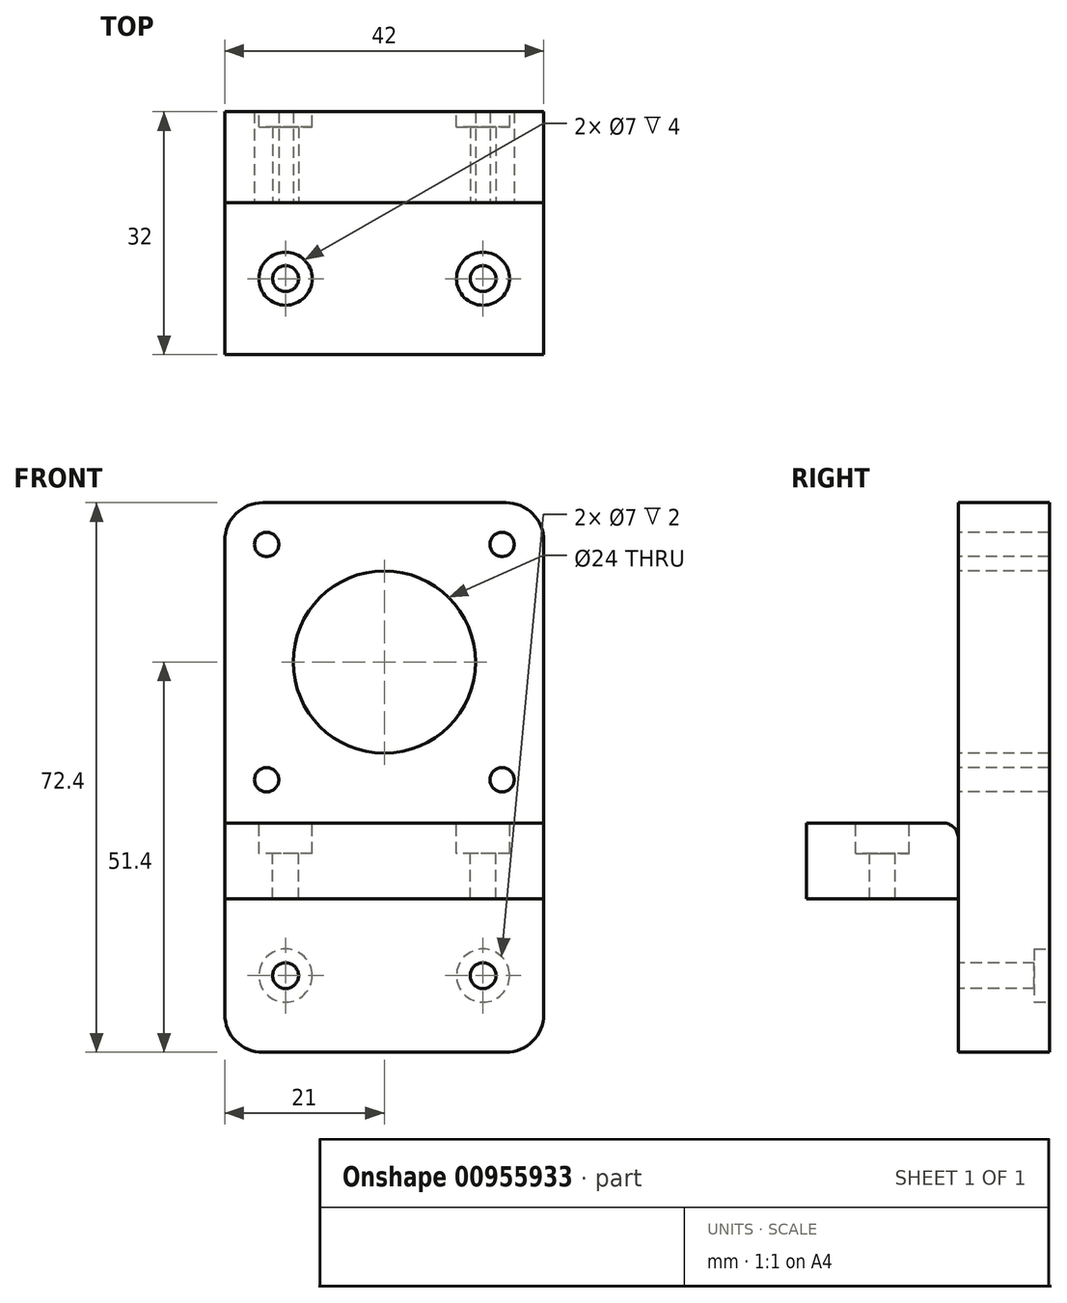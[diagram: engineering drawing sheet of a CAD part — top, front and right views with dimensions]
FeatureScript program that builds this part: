
annotation { "Feature Type Name" : "Feature", "Feature Type Description" : "" }
export const myFeature = defineFeature(function(context is Context, id is Id, definition is map)
    precondition{}
    {
        {
            var Q0;
            Q0=qCreatedBy(makeId("Front.planeOp"),FACE);
            var sketch = newSketch(context, id + "F0", { "sketchPlane" : qUnion([Q0])});
            skLineSegment(sketch, "E0.bottom", {"start": v(-21, 21) * mm, "end": v(21, 21) * mm});
            skLineSegment(sketch, "E0.left", {"start": v(-21, 21) * mm, "end": v(-21, -21) * mm});
            skLineSegment(sketch, "E0.right", {"start": v(21, 21) * mm, "end": v(21, -21) * mm});
            skPoint(sketch, "E0.middle", {"position": v(0, 0) * mm});
            skLineSegment(sketch, "E1", {"start": v(0, 0) * mm, "end": v(15.5, 0) * mm, "construction": true});
            skLineSegment(sketch, "E2", {"start": v(0, 0) * mm, "end": v(0, 15.5) * mm, "construction": true});
            skLineSegment(sketch, "E3", {"start": v(15.5, -21) * mm, "end": v(15.5, 21) * mm, "construction": true});
            skLineSegment(sketch, "E4", {"start": v(21, 15.5) * mm, "end": v(-21, 15.5) * mm, "construction": true});
            skLineSegment(sketch, "E5", {"start": v(0, 0) * mm, "end": v(-15.5, 0) * mm, "construction": true});
            skLineSegment(sketch, "E6", {"start": v(0, 0) * mm, "end": v(0, -15.5) * mm, "construction": true});
            skLineSegment(sketch, "E7", {"start": v(-15.5, 21) * mm, "end": v(-15.5, -21) * mm, "construction": true});
            skLineSegment(sketch, "E8", {"start": v(21, -15.5) * mm, "end": v(-21, -15.5) * mm, "construction": true});
            skCircle(sketch, "E9", {"center": v(-15.5, 15.5) * mm, "radius": 1.6 * mm});
            skCircle(sketch, "E10", {"center": v(15.5, 15.5) * mm, "radius": 1.6 * mm});
            skCircle(sketch, "E11", {"center": v(15.5, -15.5) * mm, "radius": 1.6 * mm});
            skCircle(sketch, "E12", {"center": v(-15.5, -15.5) * mm, "radius": 1.6 * mm});
            skLineSegment(sketch, "E13", {"start": v(-21, -21) * mm, "end": v(21, -21) * mm});
            skLineSegment(sketch, "E14.0", {"start": v(-21, -21.2) * mm, "end": v(21, -21.2) * mm});
            skLineSegment(sketch, "E15", {"start": v(21, -21.2) * mm, "end": v(21, -31.2) * mm});
            skLineSegment(sketch, "E16", {"start": v(-21, -31.2) * mm, "end": v(21, -31.2) * mm});
            skLineSegment(sketch, "E17.bottom", {"start": v(-21.2, 21) * mm, "end": v(21, 21) * mm});
            skLineSegment(sketch, "E17.right", {"start": v(21, 21) * mm, "end": v(21, -31.2) * mm});
            skCircle(sketch, "E18", {"center": v(0, 0) * mm, "radius": 12 * mm});
            skLineSegment(sketch, "E19.top", {"start": v(21, -51.4) * mm, "end": v(-21, -51.4) * mm});
            skLineSegment(sketch, "E19.left", {"start": v(21, -31.2) * mm, "end": v(21, -51.4) * mm});
            skLineSegment(sketch, "E20", {"start": v(21, -31.2) * mm, "end": v(21, -31.4) * mm, "construction": true});
            skLineSegment(sketch, "E21", {"start": v(21, -31.4) * mm, "end": v(-21, -31.4) * mm, "construction": true});
            skLineSegment(sketch, "E22", {"start": v(0, -41.3) * mm, "end": v(13, -41.3) * mm, "construction": true});
            skPoint(sketch, "E22.startSnap0", {"position": v(21, -41.3) * mm});
            skLineSegment(sketch, "E23", {"start": v(0, -41.3) * mm, "end": v(-13, -41.3) * mm, "construction": true});
            skCircle(sketch, "E24", {"center": v(13, -41.3) * mm, "radius": 1.7 * mm});
            skCircle(sketch, "E25", {"center": v(-13, -41.3) * mm, "radius": 1.7 * mm});
            skCircle(sketch, "E26", {"center": v(13, -41.3) * mm, "radius": 3.5 * mm});
            skCircle(sketch, "E27", {"center": v(-13, -41.3) * mm, "radius": 3.5 * mm});
            skLineSegment(sketch, "E28", {"start": v(-21, -21) * mm, "end": v(-21, -51.4) * mm});
            skSolve(sketch);
        }
        {
            var Q0;
            {var subQ0=sQuery(id+"F0.wireOp",EDGE,"E14.0");Q0=makeQuery(id+"F0.imprint","IMPRINT",FACE,{"disambiguationData":[TD([[makeQuery(id+"F0.imprint","IMPRINT",EDGE,{"derivedFrom":subQ0}),-1.0]])]});}
            extrude(context, id + "F1", {"entities" : qUnion([Q0]), "depth" : 20 * mm});
        }
        {
            var Q0;
            {var subQ3=sQuery(id+"F0.wireOp",EDGE,"E0.left");Q0=makeQuery(id+"F0.imprint","IMPRINT",FACE,{"disambiguationData":[TD([[makeQuery(id+"F0.imprint","IMPRINT",EDGE,{"derivedFrom":subQ3}),-1.0]])]});}
            var Q1;
            {var subQ0=sQuery(id+"F0.wireOp",EDGE,"E14.0");Q1=makeQuery(id+"F0.imprint","IMPRINT",FACE,{"disambiguationData":[TD([[makeQuery(id+"F0.imprint","IMPRINT",EDGE,{"derivedFrom":subQ0}),-1.0]])]});}
            var Q2;
            Q2=makeQuery(id+"F0.imprint","IMPRINT",FACE,{"disambiguationData":[TD([[makeQuery(id+"F0.imprint","IMPRINT",EDGE,{"derivedFrom":sQuery(id+"F0.wireOp",EDGE,"E0.bottom")}),-1.0]])]});
            var Q3;
            {var subQ1=sQuery(id+"F0.wireOp",EDGE,"E16");Q3=makeQuery(id+"F0.imprint","IMPRINT",FACE,{"disambiguationData":[TD([[makeQuery(id+"F0.imprint","IMPRINT",EDGE,{"derivedFrom":subQ1}),-1.0]])]});}
            var Q4;
            {var subQ0=sQuery(id+"F0.wireOp",EDGE,"E13");Q4=makeQuery(id+"F0.imprint","IMPRINT",FACE,{"disambiguationData":[TD([[makeQuery(id+"F0.imprint","IMPRINT",EDGE,{"derivedFrom":subQ0}),-1.0]])]});}
            extrude(context, id + "F2", {"entities" : qUnion([Q0, Q1, Q2, Q3, Q4]), "oppositeDirection" : true, "depth" : 12 * mm});
        }
        {
            var Q0;
            Q0=makeQuery(id+"F1.opExtrude","SWEPT_FACE",FACE,{"disambiguationData":[OSD([sQuery(id+"F0.wireOp",EDGE,"E14.0")])]});
            var sketch = newSketch(context, id + "F3", { "sketchPlane" : qUnion([Q0])});
            skLineSegment(sketch, "E29", {"start": v(0, 0) * mm, "end": v(0, -20) * mm, "construction": true});
            skLineSegment(sketch, "E30", {"start": v(0, -10) * mm, "end": v(13, -10) * mm, "construction": true});
            skPoint(sketch, "E30.endSnap0", {"position": v(0, -10) * mm});
            skLineSegment(sketch, "E31", {"start": v(0, -10) * mm, "end": v(-13, -10) * mm, "construction": true});
            skCircle(sketch, "E32", {"center": v(-13, -10) * mm, "radius": 1.7 * mm});
            skCircle(sketch, "E33", {"center": v(13, -10) * mm, "radius": 1.7 * mm});
            skCircle(sketch, "E34", {"center": v(-13, -10) * mm, "radius": 3.5 * mm});
            skCircle(sketch, "E35", {"center": v(13, -10) * mm, "radius": 3.5 * mm});
            skSolve(sketch);
        }
        {
            var Q0;
            Q0=makeQuery(id+"F3.imprint","IMPRINT",FACE,{"disambiguationData":[TD([[makeQuery(id+"F3.imprint","IMPRINT",EDGE,{"derivedFrom":sQuery(id+"F3.wireOp",EDGE,"E32")}),1.0]])]});
            var Q1;
            Q1=makeQuery(id+"F3.imprint","IMPRINT",FACE,{"disambiguationData":[TD([[makeQuery(id+"F3.imprint","IMPRINT",EDGE,{"derivedFrom":sQuery(id+"F3.wireOp",EDGE,"E33")}),1.0]])]});
            extrude(context, id + "F4", {"entities" : qUnion([Q0, Q1]), "operationType" : NewBodyOperationType.REMOVE, "oppositeDirection" : true, "depth" : 25 * mm});
        }
        {
            var Q0;
            Q0=makeQuery(id+"F3.imprint","IMPRINT",FACE,{"disambiguationData":[TD([[makeQuery(id+"F3.imprint","IMPRINT",EDGE,{"derivedFrom":sQuery(id+"F3.wireOp",EDGE,"E32")}),-1.0]])]});
            var Q1;
            Q1=makeQuery(id+"F3.imprint","IMPRINT",FACE,{"disambiguationData":[TD([[makeQuery(id+"F3.imprint","IMPRINT",EDGE,{"derivedFrom":sQuery(id+"F3.wireOp",EDGE,"E33")}),-1.0]])]});
            extrude(context, id + "F5", {"entities" : qUnion([Q0, Q1]), "operationType" : NewBodyOperationType.REMOVE, "oppositeDirection" : true, "depth" : 4 * mm});
        }
        {
            var Q0;
            Q0=makeQuery(id+"F0.imprint","IMPRINT",FACE,{"disambiguationData":[TD([[makeQuery(id+"F0.imprint","IMPRINT",EDGE,{"derivedFrom":sQuery(id+"F0.wireOp",EDGE,"E19.bottom")}),1.0]])]});
            var Q1;
            Q1=makeQuery(id+"F0.imprint","IMPRINT",FACE,{"disambiguationData":[TD([[makeQuery(id+"F0.imprint","IMPRINT",EDGE,{"derivedFrom":sQuery(id+"F0.wireOp",EDGE,"E24")}),-1.0]])]});
            var Q2;
            Q2=makeQuery(id+"F0.imprint","IMPRINT",FACE,{"disambiguationData":[TD([[makeQuery(id+"F0.imprint","IMPRINT",EDGE,{"derivedFrom":sQuery(id+"F0.wireOp",EDGE,"E25")}),-1.0]])]});
            extrude(context, id + "F6", {"entities" : qUnion([Q0, Q1, Q2]), "operationType" : NewBodyOperationType.ADD, "oppositeDirection" : true, "depth" : 12 * mm});
        }
        {
            var Q0;
            {var subQ0=sQuery(id+"F0.wireOp",EDGE,"E27");var subQ1=sQuery(id+"F0.wireOp",EDGE,"E26");Q0=makeQuery(id+"F6.boolean.opBoolean","MERGE",FACE,{"derivedFrom":[makeQuery(id+"F2.opExtrude","CAP_FACE",FACE,{"disambiguationData":[OSD([sQuery(id+"F0.wireOp",EDGE,"E0.bottom"),sQuery(id+"F0.wireOp",EDGE,"E0.left"),sQuery(id+"F0.wireOp",EDGE,"E0.right"),sQuery(id+"F0.wireOp",EDGE,"E9"),sQuery(id+"F0.wireOp",EDGE,"E10"),sQuery(id+"F0.wireOp",EDGE,"E11"),sQuery(id+"F0.wireOp",EDGE,"E12"),sQuery(id+"F0.wireOp",EDGE,"E15"),sQuery(id+"F0.wireOp",EDGE,"E17.right"),sQuery(id+"F0.wireOp",EDGE,"E18"),sQuery(id+"F0.wireOp",EDGE,"E19.top"),sQuery(id+"F0.wireOp",EDGE,"E19.left"),subQ1,subQ0,sQuery(id+"F0.wireOp",EDGE,"E28")])],"isStart":false}),makeQuery(id+"F6.opExtrude","CAP_FACE",FACE,{"disambiguationData":[OSD([sQuery(id+"F0.wireOp",EDGE,"E24"),subQ1])],"isStart":false}),makeQuery(id+"F6.opExtrude","CAP_FACE",FACE,{"disambiguationData":[OSD([sQuery(id+"F0.wireOp",EDGE,"E25"),subQ0])],"isStart":false})]});}
            var sketch = newSketch(context, id + "F7", { "sketchPlane" : qUnion([Q0])});
            skCircle(sketch, "E36", {"center": v(-13, -41.3) * mm, "radius": 3.5 * mm});
            skCircle(sketch, "E37", {"center": v(13, -41.3) * mm, "radius": 3.5 * mm});
            skSolve(sketch);
        }
        {
            var Q0;
            Q0=makeQuery(id+"F7.imprint","IMPRINT",FACE,{"disambiguationData":[TD([[makeQuery(id+"F7.imprint","IMPRINT",EDGE,{"derivedFrom":sQuery(id+"F7.wireOp",EDGE,"E36")}),1.0]])]});
            var Q1;
            Q1=makeQuery(id+"F7.imprint","IMPRINT",FACE,{"disambiguationData":[TD([[makeQuery(id+"F7.imprint","IMPRINT",EDGE,{"derivedFrom":sQuery(id+"F7.wireOp",EDGE,"E37")}),1.0]])]});
            extrude(context, id + "F8", {"entities" : qUnion([Q0, Q1]), "operationType" : NewBodyOperationType.REMOVE, "oppositeDirection" : true, "depth" : 2 * mm});
        }
        {
            var Q0;
            Q0=makeQuery(id+"F2.opExtrude","SWEPT_EDGE",EDGE,{"disambiguationData":[OSD([sQuery(id+"F0.wireOp",EDGE,"E0.bottom"),sQuery(id+"F0.wireOp",EDGE,"E0.right")])]});
            var Q1;
            Q1=makeQuery(id+"F2.opExtrude","SWEPT_EDGE",EDGE,{"disambiguationData":[OSD([sQuery(id+"F0.wireOp",EDGE,"E0.bottom"),sQuery(id+"F0.wireOp",EDGE,"E0.left")])]});
            var Q2;
            Q2=makeQuery(id+"F2.opExtrude","SWEPT_EDGE",EDGE,{"disambiguationData":[OSD([sQuery(id+"F0.wireOp",EDGE,"E19.top"),sQuery(id+"F0.wireOp",EDGE,"E28")])]});
            var Q3;
            Q3=makeQuery(id+"F2.opExtrude","SWEPT_EDGE",EDGE,{"disambiguationData":[OSD([sQuery(id+"F0.wireOp",EDGE,"E19.top"),sQuery(id+"F0.wireOp",EDGE,"E19.left")])]});
            fillet(context, id + "F9", {"entities" : qUnion([Q0, Q1, Q2, Q3]), "radius" : 5 * mm, "tangentPropagation" : true, "allowEdgeOverflow" : false});
        }
        {
            var Q0;
            Q0=makeQuery(id+"F1.opExtrude","CAP_EDGE",EDGE,{"disambiguationData":[OSD([sQuery(id+"F0.wireOp",EDGE,"E14.0")])],"isStart":true});
            fillet(context, id + "F10", {"entities" : qUnion([Q0]), "radius" : 2 * mm, "tangentPropagation" : true, "allowEdgeOverflow" : false});
        }
    });
